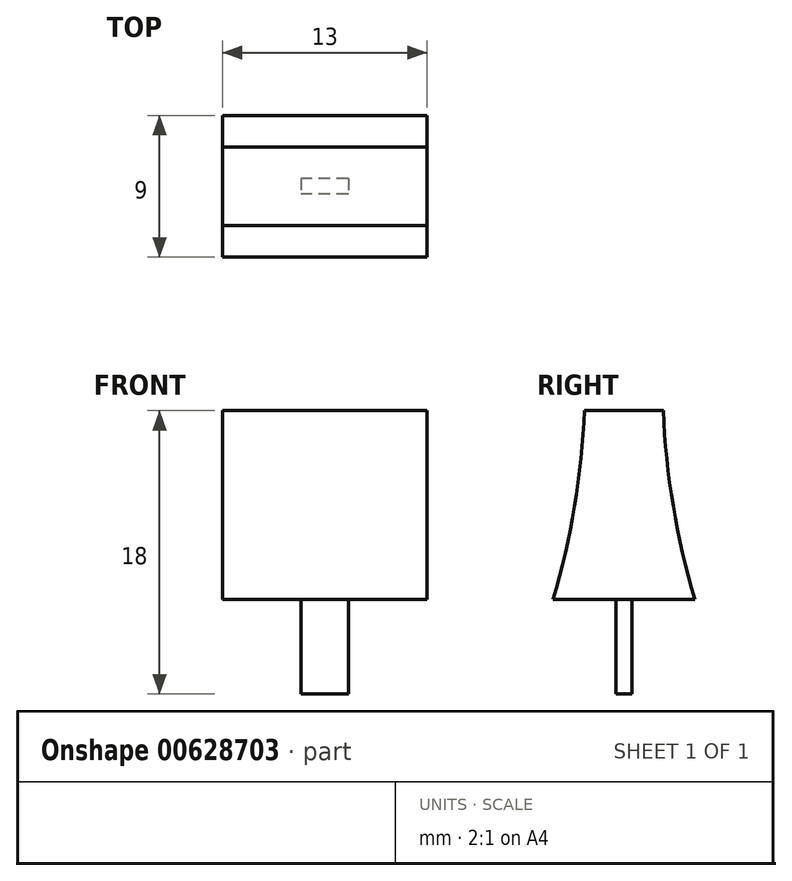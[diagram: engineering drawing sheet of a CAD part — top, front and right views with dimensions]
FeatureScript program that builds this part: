
annotation { "Feature Type Name" : "Feature", "Feature Type Description" : "" }
export const myFeature = defineFeature(function(context is Context, id is Id, definition is map)
    precondition{}
    {
        {
            var Q0;
            Q0=qCreatedBy(makeId("Top.planeOp"),FACE);
            var sketch = newSketch(context, id + "F0", { "sketchPlane" : qUnion([Q0])});
            skLineSegment(sketch, "E0.bottom", {"start": v(1.5, 0.5) * mm, "end": v(-1.5, 0.5) * mm});
            skLineSegment(sketch, "E0.top", {"start": v(1.5, -0.5) * mm, "end": v(-1.5, -0.5) * mm});
            skLineSegment(sketch, "E0.left", {"start": v(1.5, 0.5) * mm, "end": v(1.5, -0.5) * mm});
            skLineSegment(sketch, "E0.right", {"start": v(-1.5, 0.5) * mm, "end": v(-1.5, -0.5) * mm});
            skPoint(sketch, "E0.middle", {"position": v(0, 0) * mm});
            skSolve(sketch);
        }
        {
            var Q0;
            Q0 = qSketchRegion(id + "F0", true);
            extrude(context, id + "F1", {"entities" : qUnion([Q0]), "depth" : 6 * mm, "offsetDistance" : 25 * mm});
        }
        {
            var Q0;
            Q0=qCreatedBy(makeId("Right.planeOp"),FACE);
            var sketch = newSketch(context, id + "F2", { "sketchPlane" : qUnion([Q0])});
            skLineSegment(sketch, "E1", {"start": v(4.5, 6) * mm, "end": v(-4.5, 6) * mm});
            skLineSegment(sketch, "E2", {"start": v(-2.5, 18) * mm, "end": v(2.5, 18) * mm});
            skArc(sketch, "E3", {"start": v(-4.5, 6) * mm, "mid": v(-3.13, 11.94) * mm, "end": v(-2.5, 18) * mm});
            skArc(sketch, "E4", {"start": v(2.5, 18) * mm, "mid": v(3.13, 11.94) * mm, "end": v(4.5, 6) * mm});
            skSolve(sketch);
        }
        {
            var Q0;
            Q0 = qSketchRegion(id + "F2", true);
            extrude(context, id + "F3", {"entities" : qUnion([Q0]), "operationType" : NewBodyOperationType.ADD, "endBound" : BoundingType.SYMMETRIC, "depth" : 13 * mm, "offsetDistance" : 25 * mm});
        }
    });
